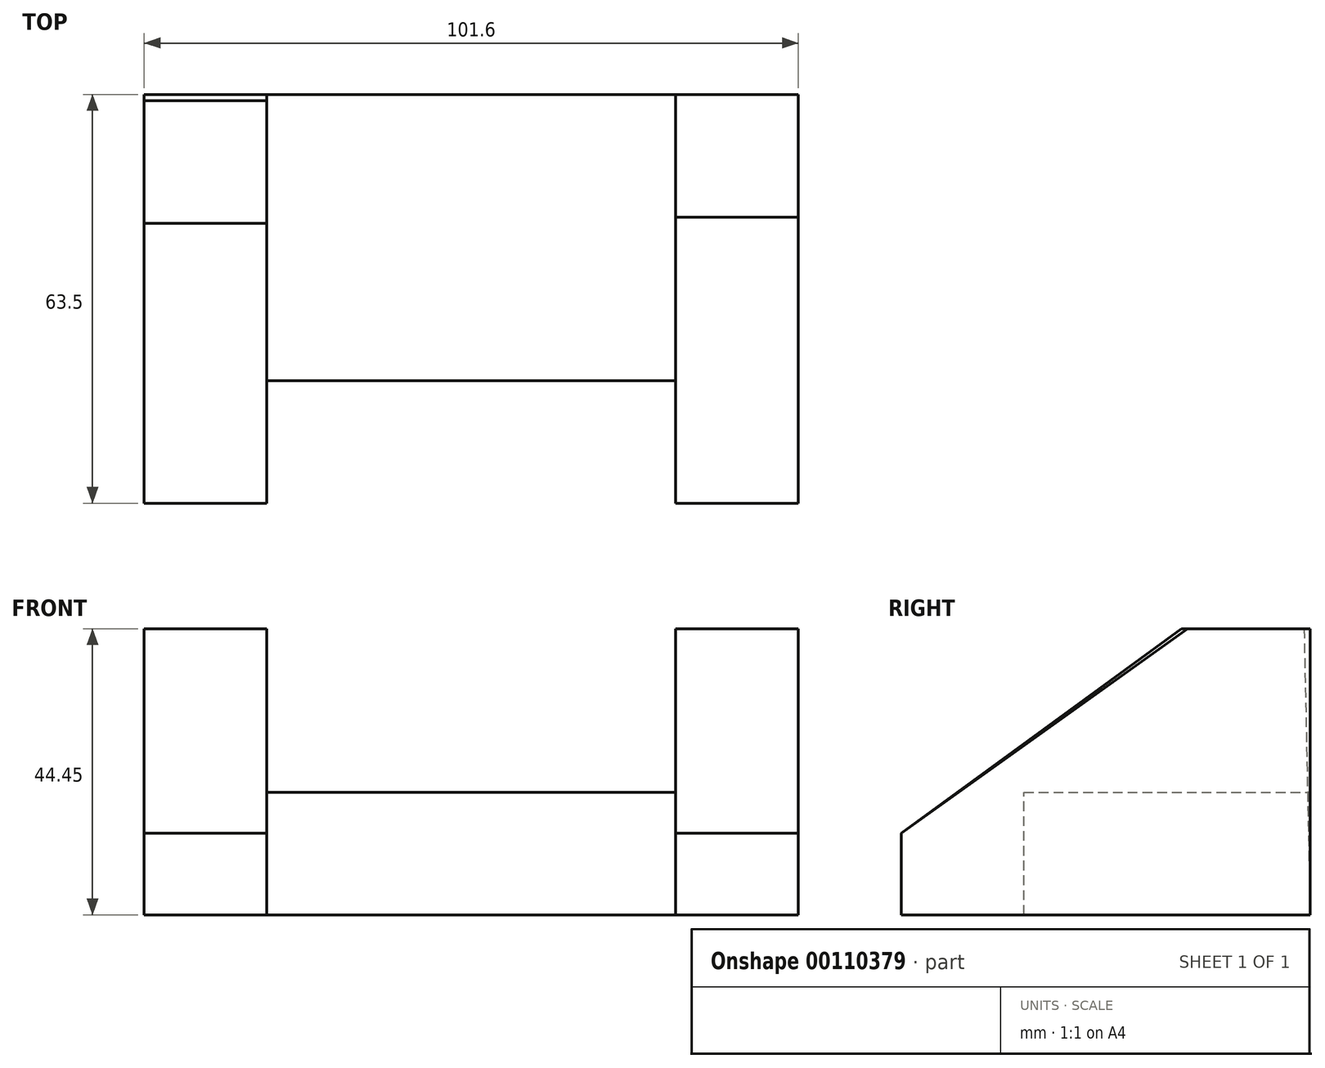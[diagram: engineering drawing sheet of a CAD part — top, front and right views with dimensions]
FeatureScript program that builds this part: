
annotation { "Feature Type Name" : "Feature", "Feature Type Description" : "" }
export const myFeature = defineFeature(function(context is Context, id is Id, definition is map)
    precondition{}
    {
        {
            var Q0;
            Q0=qCreatedBy(makeId("Right.planeOp"),FACE);
            var sketch = newSketch(context, id + "F0", { "sketchPlane" : qUnion([Q0])});
            skLineSegment(sketch, "E0", {"start": v(-43.5, -11.39) * mm, "end": v(-43.5, -24.09) * mm});
            skLineSegment(sketch, "E1", {"start": v(-43.5, -24.09) * mm, "end": v(20, -24.09) * mm});
            skLineSegment(sketch, "E2", {"start": v(20, -24.09) * mm, "end": v(20, 20.36) * mm});
            skLineSegment(sketch, "E3", {"start": v(20, 20.36) * mm, "end": v(0.96, 20.36) * mm});
            skLineSegment(sketch, "E4", {"start": v(0.96, 20.36) * mm, "end": v(-43.5, -11.39) * mm});
            skSolve(sketch);
        }
        {
            var Q0;
            Q0 = qSketchRegion(id + "F0", true);
            extrude(context, id + "F1", {"entities" : qUnion([Q0]), "depth" : 19.05 * mm});
        }
        {
            var Q0;
            Q0=makeQuery(id+"F1.opExtrude","CAP_FACE",FACE,{"disambiguationData":[OSD([sQuery(id+"F0.wireOp",EDGE,"E0"),sQuery(id+"F0.wireOp",EDGE,"E1"),sQuery(id+"F0.wireOp",EDGE,"E2"),sQuery(id+"F0.wireOp",EDGE,"E3"),sQuery(id+"F0.wireOp",EDGE,"E4")])],"isStart":true});
            var sketch = newSketch(context, id + "F2", { "sketchPlane" : qUnion([Q0])});
            skLineSegment(sketch, "E5", {"start": v(-20, -24.09) * mm, "end": v(24.44, -24.09) * mm});
            skLineSegment(sketch, "E6", {"start": v(24.44, -24.09) * mm, "end": v(24.44, -5.04) * mm});
            skLineSegment(sketch, "E7", {"start": v(24.44, -5.04) * mm, "end": v(-20, -5.04) * mm});
            skLineSegment(sketch, "E8", {"start": v(-20, -5.04) * mm, "end": v(-20, -24.09) * mm});
            skSolve(sketch);
        }
        {
            var Q0;
            Q0=makeQuery(id+"F2.imprint","IMPRINT",FACE,{"disambiguationData":[TD([[makeQuery(id+"F2.imprint","IMPRINT",EDGE,{"derivedFrom":sQuery(id+"F2.wireOp",EDGE,"E5")}),-1.0]])]});
            extrude(context, id + "F3", {"entities" : qUnion([Q0]), "operationType" : NewBodyOperationType.ADD, "depth" : 63.5 * mm});
        }
        {
            var Q0;
            Q0=makeQuery(id+"F3.opExtrude","CAP_FACE",FACE,{"disambiguationData":[OSD([sQuery(id+"F2.wireOp",EDGE,"E5"),sQuery(id+"F2.wireOp",EDGE,"E6"),sQuery(id+"F2.wireOp",EDGE,"E7"),sQuery(id+"F2.wireOp",EDGE,"E8")])],"isStart":false});
            var sketch = newSketch(context, id + "F4", { "sketchPlane" : qUnion([Q0])});
            skLineSegment(sketch, "E9", {"start": v(-20, -24.09) * mm, "end": v(43.5, -24.09) * mm});
            skLineSegment(sketch, "E10", {"start": v(43.5, -24.09) * mm, "end": v(43.5, -11.39) * mm});
            skLineSegment(sketch, "E11", {"start": v(43.5, -11.39) * mm, "end": v(0, 20.36) * mm});
            skLineSegment(sketch, "E12", {"start": v(0, 20.36) * mm, "end": v(-19.05, 20.36) * mm});
            skLineSegment(sketch, "E13", {"start": v(-19.05, 20.36) * mm, "end": v(-20, -24.09) * mm});
            skSolve(sketch);
        }
        {
            var Q0;
            {var subQ5=sQuery(id+"F4.wireOp",EDGE,"E10");Q0=makeQuery(id+"F4.imprint","IMPRINT",FACE,{"disambiguationData":[TD([[makeQuery(id+"F4.imprint","IMPRINT",EDGE,{"derivedFrom":subQ5}),1.0]])]});}
            var Q1;
            {var subQ3=makeQuery(id+"F3.opExtrude","CAP_EDGE",EDGE,{"disambiguationData":[OSD([sQuery(id+"F2.wireOp",EDGE,"E6")])],"isStart":false});Q1=makeQuery(id+"F4.imprint","IMPRINT",FACE,{"disambiguationData":[TD([[makeQuery(id+"F4.imprint","IMPRINT",EDGE,{"derivedFrom":subQ3}),1.0]])]});}
            extrude(context, id + "F5", {"entities" : qUnion([Q0, Q1]), "operationType" : NewBodyOperationType.ADD, "depth" : 19.05 * mm});
        }
    });
